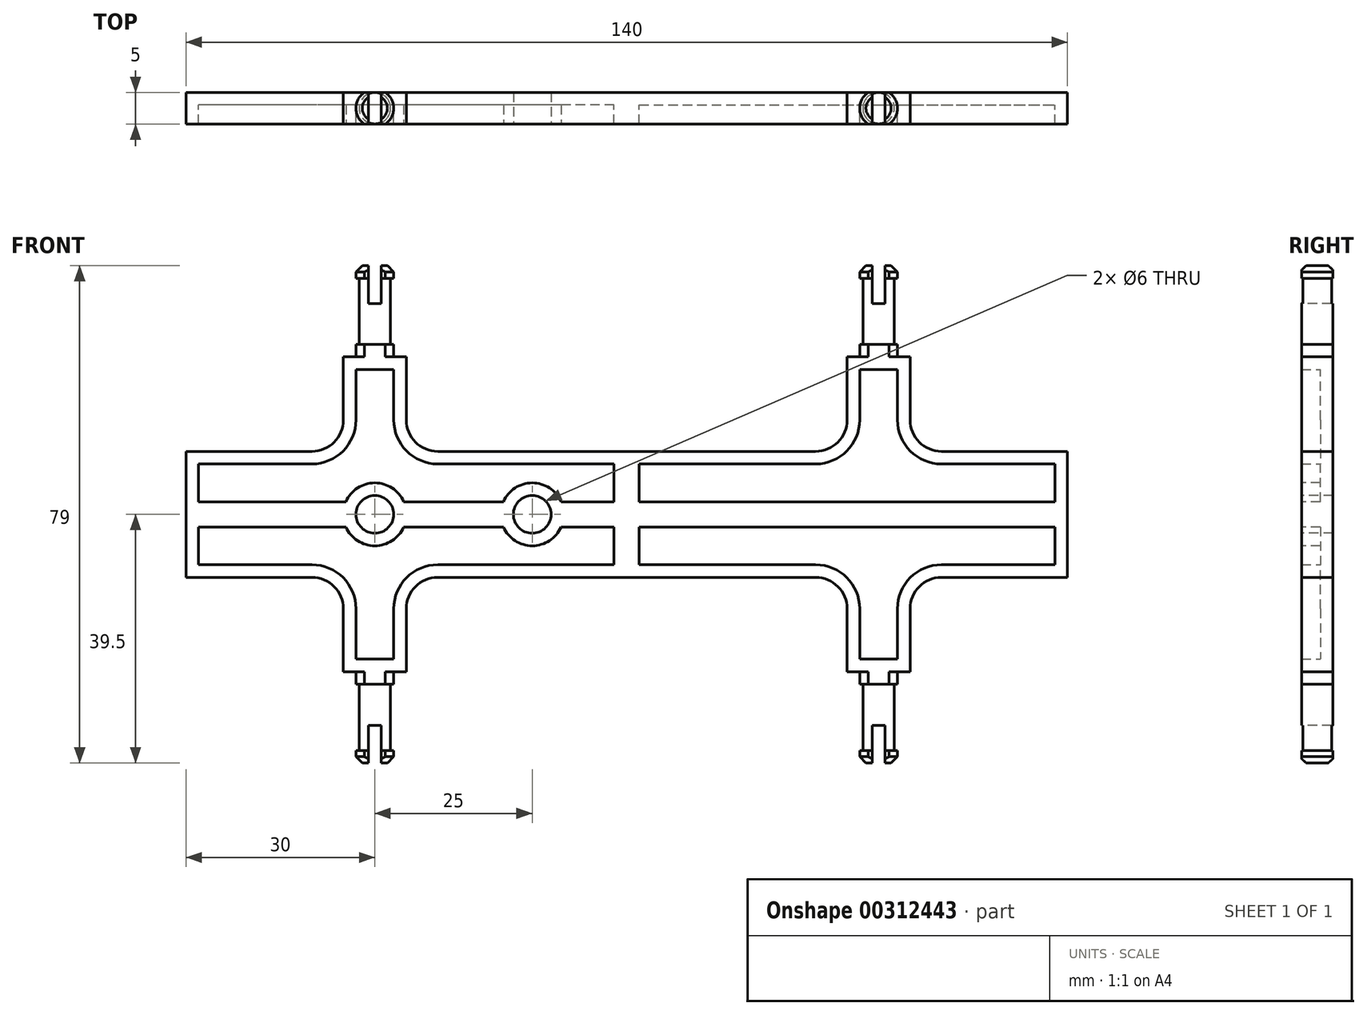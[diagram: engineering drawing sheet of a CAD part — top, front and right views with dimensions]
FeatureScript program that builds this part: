
annotation { "Feature Type Name" : "Feature", "Feature Type Description" : "" }
export const myFeature = defineFeature(function(context is Context, id is Id, definition is map)
    precondition{}
    {
        {
            var Q0;
            Q0=qCreatedBy(makeId("Front.planeOp"),FACE);
            var sketch = newSketch(context, id + "F0", { "sketchPlane" : qUnion([Q0])});
            skLineSegment(sketch, "E0.bottom", {"start": v(0, 0) * mm, "end": v(70, 0) * mm});
            skLineSegment(sketch, "E0.top", {"start": v(0, 10) * mm, "end": v(8.4, 10) * mm});
            skLineSegment(sketch, "E0.left", {"start": v(0, 0) * mm, "end": v(0, 10) * mm});
            skLineSegment(sketch, "E0.right", {"start": v(70, 0) * mm, "end": v(70, 10) * mm});
            skLineSegment(sketch, "E1.top", {"start": v(35, 25) * mm, "end": v(45, 25) * mm});
            skLineSegment(sketch, "E1.left", {"start": v(35, 15) * mm, "end": v(35, 25) * mm});
            skLineSegment(sketch, "E1.right", {"start": v(45, 15) * mm, "end": v(45, 25) * mm});
            skLineSegment(sketch, "E2", {"start": v(8.4, 10) * mm, "end": v(30, 10) * mm});
            skLineSegment(sketch, "E3", {"start": v(45, 15) * mm, "end": v(45, 15) * mm});
            skLineSegment(sketch, "E4", {"start": v(35, 15) * mm, "end": v(35, 15) * mm});
            skLineSegment(sketch, "E5.trimOffspring", {"start": v(50, 10) * mm, "end": v(70, 10) * mm});
            skPoint(sketch, "E6.visualSharp", {"position": v(45, 10) * mm});
            skArc(sketch, "E6.filletArc", {"start": v(45, 15) * mm, "mid": v(46.46, 11.46) * mm, "end": v(50, 10) * mm});
            skPoint(sketch, "E7.visualSharp", {"position": v(35, 10) * mm});
            skArc(sketch, "E7.filletArc", {"start": v(30, 10) * mm, "mid": v(33.54, 11.46) * mm, "end": v(35, 15) * mm});
            skPoint(sketch, "E8.trimOffspring.end.orphan", {"position": v(24.92, 10) * mm});
            skSolve(sketch);
        }
        {
            var Q0;
            Q0=makeQuery(id+"F0.imprint","IMPRINT",FACE,{"disambiguationData":[TD([[makeQuery(id+"F0.imprint","IMPRINT",EDGE,{"derivedFrom":sQuery(id+"F0.wireOp",EDGE,"E0.bottom")}),1.0]])]});
            extrude(context, id + "F1", {"entities" : qUnion([Q0]), "endBound" : BoundingType.SYMMETRIC, "depth" : 5 * mm});
        }
        {
            var Q0;
            Q0=makeQuery(id+"F1.opExtrude","CAP_FACE",FACE,{"disambiguationData":[OSD([sQuery(id+"F0.wireOp",EDGE,"E0.bottom"),sQuery(id+"F0.wireOp",EDGE,"E0.top"),sQuery(id+"F0.wireOp",EDGE,"E0.left"),sQuery(id+"F0.wireOp",EDGE,"E0.right"),sQuery(id+"F0.wireOp",EDGE,"E1.top"),sQuery(id+"F0.wireOp",EDGE,"E1.left"),sQuery(id+"F0.wireOp",EDGE,"E1.right"),sQuery(id+"F0.wireOp",EDGE,"E2"),sQuery(id+"F0.wireOp",EDGE,"E5.trimOffspring"),sQuery(id+"F0.wireOp",EDGE,"E6.filletArc"),sQuery(id+"F0.wireOp",EDGE,"E7.filletArc")])],"isStart":false});
            shell(context, id + "F2", {"entities" : qUnion([Q0]), "thickness" : 2 * mm});
        }
        {
            var Q0;
            Q0=qCreatedBy(makeId("Front.planeOp"),FACE);
            var sketch = newSketch(context, id + "F3", { "sketchPlane" : qUnion([Q0])});
            skLineSegment(sketch, "E9", {"start": v(40, 25) * mm, "end": v(37, 25) * mm});
            skLineSegment(sketch, "E10", {"start": v(37, 25) * mm, "end": v(37, 27) * mm});
            skLineSegment(sketch, "E11", {"start": v(37, 27) * mm, "end": v(37.5, 27) * mm});
            skLineSegment(sketch, "E12", {"start": v(37.5, 27) * mm, "end": v(37.5, 37.5) * mm});
            skLineSegment(sketch, "E13", {"start": v(37.5, 37.5) * mm, "end": v(37, 37.5) * mm});
            skLineSegment(sketch, "E14", {"start": v(37, 37.5) * mm, "end": v(37, 39.5) * mm});
            skLineSegment(sketch, "E15", {"start": v(37, 39.5) * mm, "end": v(40, 39.5) * mm});
            skLineSegment(sketch, "E16", {"start": v(40, 39.5) * mm, "end": v(40, 25) * mm});
            skSolve(sketch);
        }
        {
            var Q0;
            Q0 = qSketchRegion(id + "F3", true);
            var Q1;
            Q1=sQuery(id+"F3.wireOp",EDGE,"E16");
            revolve(context, id + "F4", {"operationType" : NewBodyOperationType.ADD, "entities" : qUnion([Q0]), "axis" : qUnion([Q1]), "revolveType" : RevolveType.FULL});
        }
        {
            var Q0;
            Q0=makeQuery(id+"F4.opRevolve","SWEPT_EDGE",EDGE,{"disambiguationData":[OSD([sQuery(id+"F3.wireOp",EDGE,"E14"),sQuery(id+"F3.wireOp",EDGE,"E15")])]});
            chamfer(context, id + "F5", {"entities" : qUnion([Q0]), "width" : 1 * mm, "tangentPropagation" : true});
        }
        {
            var Q0;
            Q0=makeQuery(id+"F4.opRevolve","SWEPT_FACE",FACE,{"disambiguationData":[OSD([sQuery(id+"F3.wireOp",EDGE,"E15")])]});
            var sketch = newSketch(context, id + "F6", { "sketchPlane" : qUnion([Q0])});
            skLineSegment(sketch, "E17.bottom", {"start": v(-2.42, 2.5) * mm, "end": v(72.58, 2.5) * mm});
            skLineSegment(sketch, "E17.top", {"start": v(-2.42, -2.5) * mm, "end": v(72.58, -2.5) * mm});
            skLineSegment(sketch, "E17.left", {"start": v(-2.42, 2.5) * mm, "end": v(-2.42, -2.5) * mm});
            skLineSegment(sketch, "E17.right", {"start": v(72.58, 2.5) * mm, "end": v(72.58, -2.5) * mm});
            skSolve(sketch);
        }
        {
            var Q0;
            Q0 = qSketchRegion(id + "F6", true);
            extrude(context, id + "F7", {"entities" : qUnion([Q0]), "operationType" : NewBodyOperationType.INTERSECT, "endBound" : BoundingType.THROUGH_ALL, "oppositeDirection" : true, "depth" : 25 * mm});
        }
        {
            var Q0;
            Q0=makeQuery(id+"F4.opRevolve","SWEPT_FACE",FACE,{"disambiguationData":[OSD([sQuery(id+"F3.wireOp",EDGE,"E15")])]});
            var sketch = newSketch(context, id + "F8", { "sketchPlane" : qUnion([Q0])});
            skLineSegment(sketch, "E18.bottom", {"start": v(39, 2.95) * mm, "end": v(41, 2.95) * mm});
            skLineSegment(sketch, "E18.top", {"start": v(39, -2.95) * mm, "end": v(41, -2.95) * mm});
            skLineSegment(sketch, "E18.left", {"start": v(39, 2.95) * mm, "end": v(39, -2.95) * mm});
            skLineSegment(sketch, "E18.right", {"start": v(41, 2.95) * mm, "end": v(41, -2.95) * mm});
            skSolve(sketch);
        }
        {
            var Q0;
            Q0 = qSketchRegion(id + "F8", true);
            extrude(context, id + "F9", {"entities" : qUnion([Q0]), "operationType" : NewBodyOperationType.REMOVE, "oppositeDirection" : true, "depth" : 6 * mm});
        }
        {
            var Q0;
            Q0=makeQuery(id+"F1.opExtrude","SWEPT_BODY",BODY,{"disambiguationData":[OSD([sQuery(id+"F0.wireOp",EDGE,"E0.bottom"),sQuery(id+"F0.wireOp",EDGE,"E0.top"),sQuery(id+"F0.wireOp",EDGE,"E0.left"),sQuery(id+"F0.wireOp",EDGE,"E0.right"),sQuery(id+"F0.wireOp",EDGE,"E1.top"),sQuery(id+"F0.wireOp",EDGE,"E1.left"),sQuery(id+"F0.wireOp",EDGE,"E1.right"),sQuery(id+"F0.wireOp",EDGE,"E2"),sQuery(id+"F0.wireOp",EDGE,"E5.trimOffspring"),sQuery(id+"F0.wireOp",EDGE,"E6.filletArc"),sQuery(id+"F0.wireOp",EDGE,"E7.filletArc")])]});
            var Q1;
            Q1=qCreatedBy(makeId("Top.planeOp"),FACE);
            mirror(context, id + "F10", {"operationType" : NewBodyOperationType.ADD, "entities" : qUnion([Q0]), "mirrorPlane" : qUnion([Q1])});
        }
        {
            var Q0;
            Q0=makeQuery(id+"F1.opExtrude","SWEPT_BODY",BODY,{"disambiguationData":[OSD([sQuery(id+"F0.wireOp",EDGE,"E0.bottom"),sQuery(id+"F0.wireOp",EDGE,"E0.top"),sQuery(id+"F0.wireOp",EDGE,"E0.left"),sQuery(id+"F0.wireOp",EDGE,"E0.right"),sQuery(id+"F0.wireOp",EDGE,"E1.top"),sQuery(id+"F0.wireOp",EDGE,"E1.left"),sQuery(id+"F0.wireOp",EDGE,"E1.right"),sQuery(id+"F0.wireOp",EDGE,"E2"),sQuery(id+"F0.wireOp",EDGE,"E5.trimOffspring"),sQuery(id+"F0.wireOp",EDGE,"E6.filletArc"),sQuery(id+"F0.wireOp",EDGE,"E7.filletArc")])]});
            var Q1;
            Q1=qCreatedBy(makeId("Right.planeOp"),FACE);
            mirror(context, id + "F11", {"operationType" : NewBodyOperationType.ADD, "entities" : qUnion([Q0]), "mirrorPlane" : qUnion([Q1])});
        }
        {
            var Q0;
            {var subQ0=makeQuery(id+"F7.boolean.opBoolean","MERGE",FACE,{"derivedFrom":[makeQuery(id+"F1.opExtrude","CAP_FACE",FACE,{"disambiguationData":[OSD([sQuery(id+"F0.wireOp",EDGE,"E0.bottom"),sQuery(id+"F0.wireOp",EDGE,"E0.top"),sQuery(id+"F0.wireOp",EDGE,"E0.left"),sQuery(id+"F0.wireOp",EDGE,"E0.right"),sQuery(id+"F0.wireOp",EDGE,"E1.top"),sQuery(id+"F0.wireOp",EDGE,"E1.left"),sQuery(id+"F0.wireOp",EDGE,"E1.right"),sQuery(id+"F0.wireOp",EDGE,"E2"),sQuery(id+"F0.wireOp",EDGE,"E5.trimOffspring"),sQuery(id+"F0.wireOp",EDGE,"E6.filletArc"),sQuery(id+"F0.wireOp",EDGE,"E7.filletArc")])],"isStart":false}),makeQuery(id+"F7.boolean.toolComplement.opBoolean","COPY",FACE,{"derivedFrom":makeQuery(id+"F7.opExtrude","SWEPT_FACE",FACE,{"disambiguationData":[OSD([sQuery(id+"F6.wireOp",EDGE,"E17.top")])]})})]});var subQ1=makeQuery(id+"F10.boolean.opBoolean","MERGE",FACE,{"derivedFrom":[subQ0,makeQuery(id+"F10.opPattern","COPY",FACE,{"derivedFrom":subQ0,"instanceName":"1"})]});Q0=makeQuery(id+"F11.boolean.opBoolean","MERGE",FACE,{"derivedFrom":[subQ1,makeQuery(id+"F11.opPattern","COPY",FACE,{"derivedFrom":subQ1,"instanceName":"1"})]});}
            var sketch = newSketch(context, id + "F12", { "sketchPlane" : qUnion([Q0])});
            skCircle(sketch, "E19", {"center": v(-40, 0) * mm, "radius": 5 * mm});
            skCircle(sketch, "E20", {"center": v(-15, 0) * mm, "radius": 5 * mm});
            skSolve(sketch);
        }
        {
            var Q0;
            Q0 = qSketchRegion(id + "F12", true);
            extrude(context, id + "F13", {"entities" : qUnion([Q0]), "operationType" : NewBodyOperationType.ADD, "endBound" : BoundingType.UP_TO_NEXT, "oppositeDirection" : true, "depth" : 25 * mm});
        }
        {
            var Q0;
            {var subQ0=makeQuery(id+"F7.boolean.opBoolean","MERGE",FACE,{"derivedFrom":[makeQuery(id+"F1.opExtrude","CAP_FACE",FACE,{"disambiguationData":[OSD([sQuery(id+"F0.wireOp",EDGE,"E0.bottom"),sQuery(id+"F0.wireOp",EDGE,"E0.top"),sQuery(id+"F0.wireOp",EDGE,"E0.left"),sQuery(id+"F0.wireOp",EDGE,"E0.right"),sQuery(id+"F0.wireOp",EDGE,"E1.top"),sQuery(id+"F0.wireOp",EDGE,"E1.left"),sQuery(id+"F0.wireOp",EDGE,"E1.right"),sQuery(id+"F0.wireOp",EDGE,"E2"),sQuery(id+"F0.wireOp",EDGE,"E5.trimOffspring"),sQuery(id+"F0.wireOp",EDGE,"E6.filletArc"),sQuery(id+"F0.wireOp",EDGE,"E7.filletArc")])],"isStart":false}),makeQuery(id+"F7.boolean.toolComplement.opBoolean","COPY",FACE,{"derivedFrom":makeQuery(id+"F7.opExtrude","SWEPT_FACE",FACE,{"disambiguationData":[OSD([sQuery(id+"F6.wireOp",EDGE,"E17.top")])]})})]});var subQ1=makeQuery(id+"F10.boolean.opBoolean","MERGE",FACE,{"derivedFrom":[subQ0,makeQuery(id+"F10.opPattern","COPY",FACE,{"derivedFrom":subQ0,"instanceName":"1"})]});Q0=makeQuery(id+"F13.boolean.opBoolean","MERGE",FACE,{"derivedFrom":[makeQuery(id+"F11.boolean.opBoolean","MERGE",FACE,{"derivedFrom":[subQ1,makeQuery(id+"F11.opPattern","COPY",FACE,{"derivedFrom":subQ1,"instanceName":"1"})]}),makeQuery(id+"F13.opExtrude","CAP_FACE",FACE,{"disambiguationData":[OSD([sQuery(id+"F12.wireOp",EDGE,"E19")])],"isStart":true}),makeQuery(id+"F13.opExtrude","CAP_FACE",FACE,{"disambiguationData":[OSD([sQuery(id+"F12.wireOp",EDGE,"E20")])],"isStart":true})]});}
            var sketch = newSketch(context, id + "F14", { "sketchPlane" : qUnion([Q0])});
            skPoint(sketch, "E21", {"position": v(-40, 0) * mm});
            skPoint(sketch, "E22", {"position": v(-15, 0) * mm});
            skSolve(sketch);
        }
        {
            var Q0;
            Q0=sQuery(id+"F14.wireOp",VERTEX,"E21");
            var Q1;
            Q1=sQuery(id+"F14.wireOp",VERTEX,"E22");
            var Q2;
            Q2=makeQuery(id+"F1.opExtrude","SWEPT_BODY",BODY,{"disambiguationData":[OSD([sQuery(id+"F0.wireOp",EDGE,"E0.bottom"),sQuery(id+"F0.wireOp",EDGE,"E0.top"),sQuery(id+"F0.wireOp",EDGE,"E0.left"),sQuery(id+"F0.wireOp",EDGE,"E0.right"),sQuery(id+"F0.wireOp",EDGE,"E1.top"),sQuery(id+"F0.wireOp",EDGE,"E1.left"),sQuery(id+"F0.wireOp",EDGE,"E1.right"),sQuery(id+"F0.wireOp",EDGE,"E2"),sQuery(id+"F0.wireOp",EDGE,"E5.trimOffspring"),sQuery(id+"F0.wireOp",EDGE,"E6.filletArc"),sQuery(id+"F0.wireOp",EDGE,"E7.filletArc")])]});
            hole(context, id + "F15", {"style" : HoleStyle.SIMPLE, "endStyle" : HoleEndStyle.THROUGH, "holeDiameter" : 6 * mm, "tappedDepth" : 12 * mm, "tapClearance" : 3, "locations" : qUnion([Q0, Q1]), "scope" : qUnion([Q2])});
        }
    });
